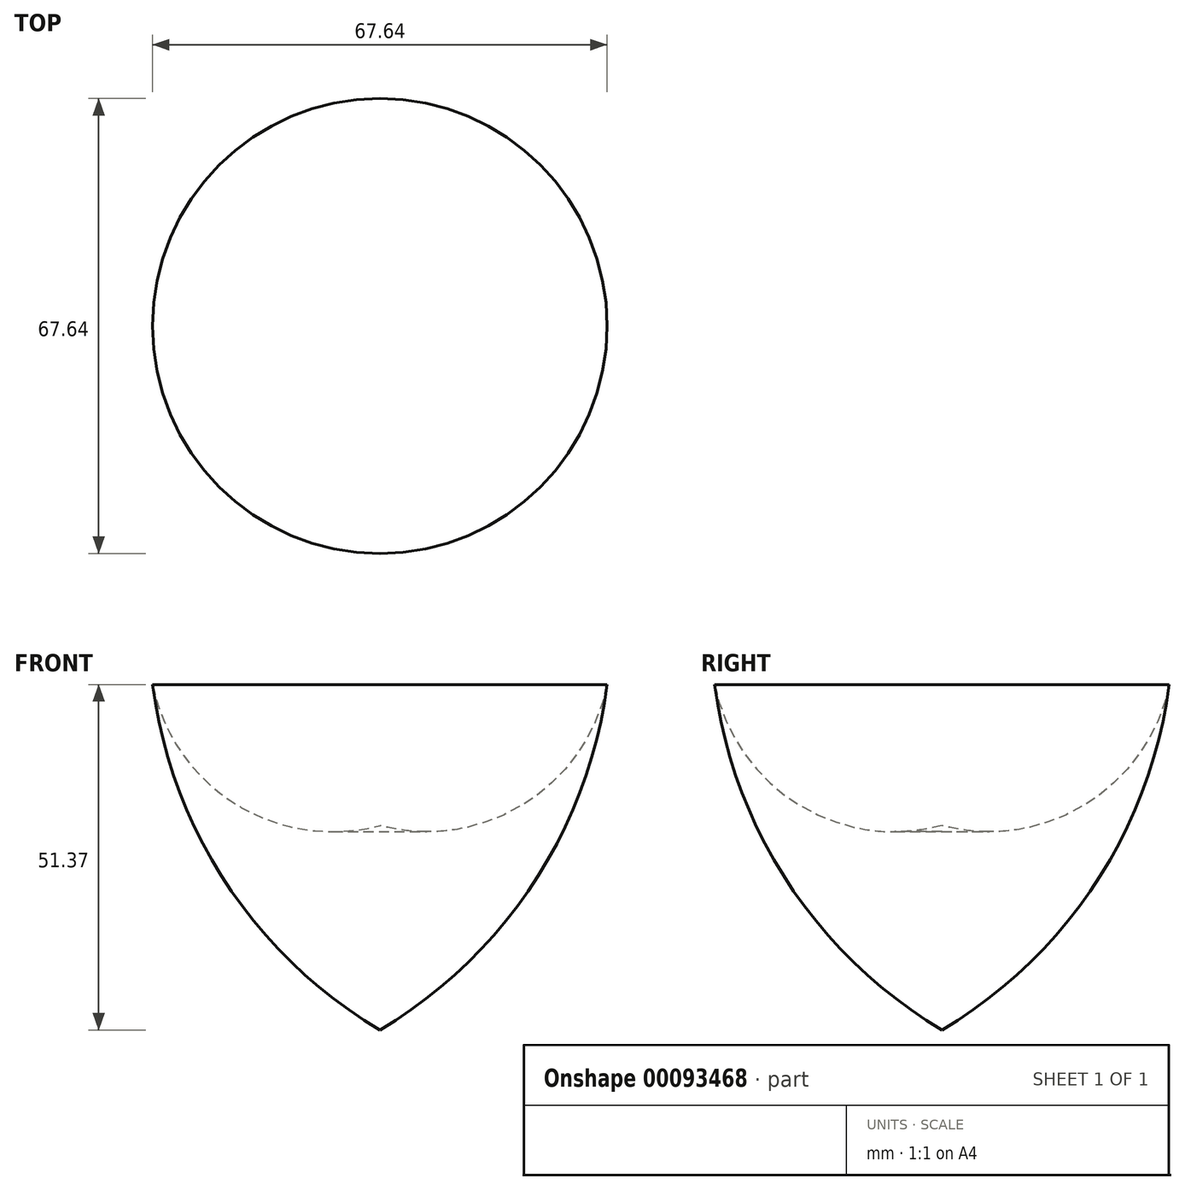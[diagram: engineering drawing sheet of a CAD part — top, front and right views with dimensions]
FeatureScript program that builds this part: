
annotation { "Feature Type Name" : "Feature", "Feature Type Description" : "" }
export const myFeature = defineFeature(function(context is Context, id is Id, definition is map)
    precondition{}
    {
        {
            var Q0;
            Q0=qCreatedBy(makeId("Front.planeOp"),FACE);
            var sketch = newSketch(context, id + "F0", { "sketchPlane" : qUnion([Q0])});
            skArc(sketch, "E0", {"start": v(33.82, 14.75) * mm, "mid": v(25.78, 40.1) * mm, "end": v(0, 46.62) * mm});
            skArc(sketch, "E1", {"start": v(0, -36.62) * mm, "mid": v(22.83, -14.83) * mm, "end": v(33.82, 14.75) * mm});
            skSolve(sketch);
        }
        {
            var Q0;
            Q0=qCreatedBy(makeId("Front.planeOp"),FACE);
            var sketch = newSketch(context, id + "F1", { "sketchPlane" : qUnion([Q0])});
            skLineSegment(sketch, "E2", {"start": v(0, 70.18) * mm, "end": v(0, -51.1) * mm});
            skSolve(sketch);
        }
        {
            var Q0;
            Q0=sQuery(id+"F0.wireOp",EDGE,"E0");
            var Q1;
            Q1=sQuery(id+"F0.wireOp",EDGE,"E1");
            var Q2;
            Q2=sQuery(id+"F1.wireOp",EDGE,"E2");
            revolve(context, id + "F2", {"bodyType" : ToolBodyType.SURFACE, "surfaceEntities" : qUnion([Q0, Q1]), "axis" : qUnion([Q2]), "revolveType" : RevolveType.FULL});
        }
    });
